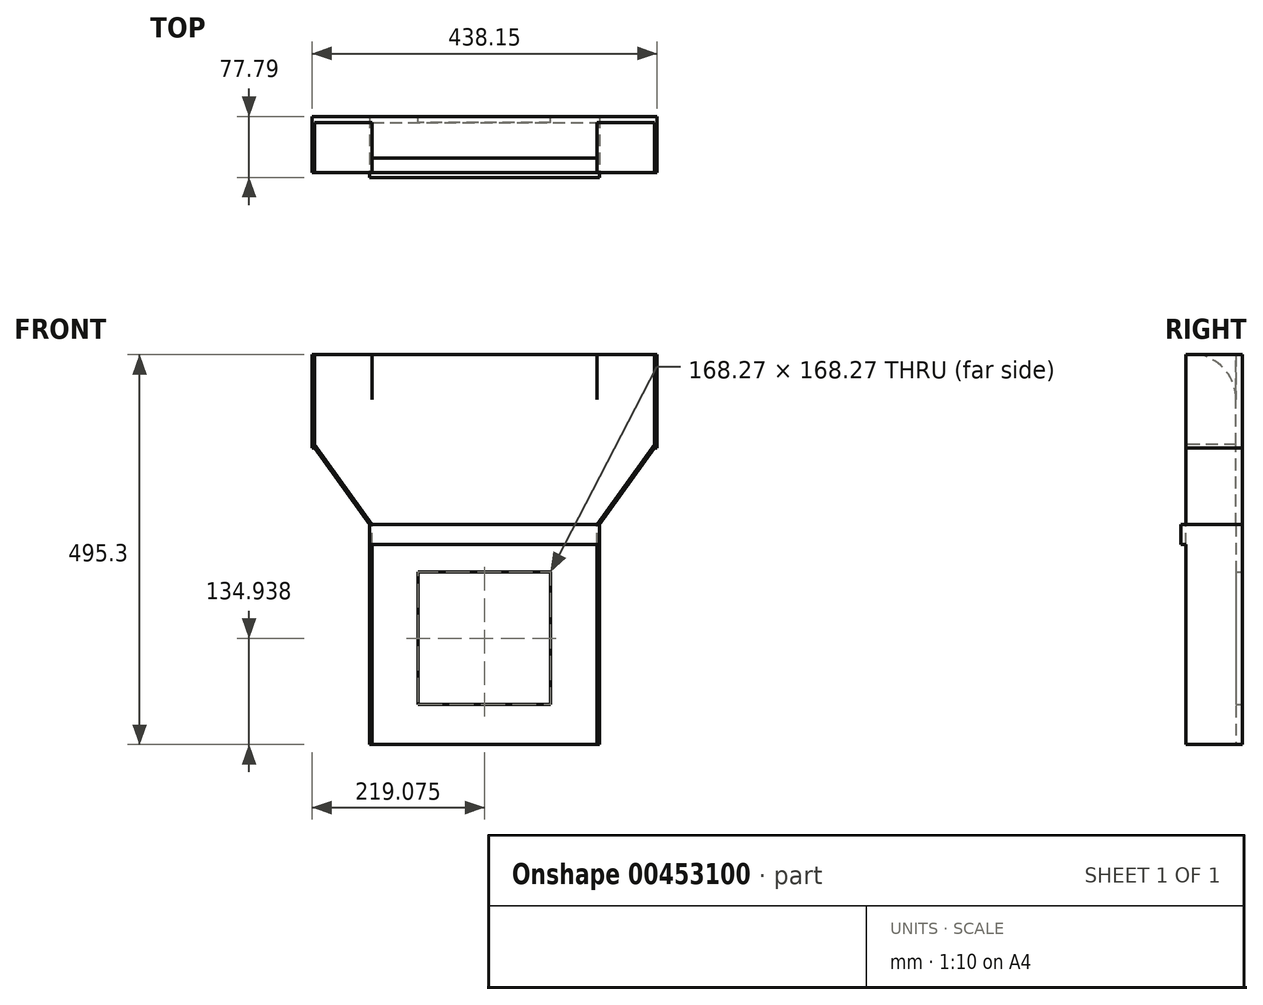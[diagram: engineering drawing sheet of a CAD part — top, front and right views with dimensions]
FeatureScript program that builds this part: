
annotation { "Feature Type Name" : "Feature", "Feature Type Description" : "" }
export const myFeature = defineFeature(function(context is Context, id is Id, definition is map)
    precondition{}
    {
        {
            var Q0;
            Q0=qCreatedBy(makeId("Front.planeOp"),FACE);
            var sketch = newSketch(context, id + "F0", { "sketchPlane" : qUnion([Q0])});
            skLineSegment(sketch, "E0.bottom", {"start": v(0, 0) * mm, "end": v(285.75, 0) * mm});
            skLineSegment(sketch, "E0.top", {"start": v(0, 279.4) * mm, "end": v(285.75, 279.4) * mm});
            skLineSegment(sketch, "E0.left", {"start": v(0, 0) * mm, "end": v(0, 279.4) * mm});
            skLineSegment(sketch, "E0.right", {"start": v(285.75, 0) * mm, "end": v(285.75, 279.4) * mm});
            skSolve(sketch);
        }
        {
            var Q0;
            Q0=makeQuery(id+"F0.imprint","IMPRINT",FACE,{"disambiguationData":[TD([[makeQuery(id+"F0.imprint","IMPRINT",EDGE,{"derivedFrom":sQuery(id+"F0.wireOp",EDGE,"E0.bottom")}),1.0]])]});
            extrude(context, id + "F1", {"entities" : qUnion([Q0]), "depth" : 3.17 * mm});
        }
        {
            var Q0;
            Q0=makeQuery(id+"F1.opExtrude","SWEPT_FACE",FACE,{"disambiguationData":[OSD([sQuery(id+"F0.wireOp",EDGE,"E0.top")])]});
            var sketch = newSketch(context, id + "F2", { "sketchPlane" : qUnion([Q0])});
            skLineSegment(sketch, "E1.bottom", {"start": v(0, 0) * mm, "end": v(285.75, 0) * mm});
            skLineSegment(sketch, "E1.top", {"start": v(0, -66.67) * mm, "end": v(285.75, -66.67) * mm});
            skLineSegment(sketch, "E1.left", {"start": v(0, 0) * mm, "end": v(0, -66.67) * mm});
            skLineSegment(sketch, "E1.right", {"start": v(285.75, 0) * mm, "end": v(285.75, -66.67) * mm});
            skSolve(sketch);
        }
        {
            var Q0;
            Q0 = qSketchRegion(id + "F2", true);
            extrude(context, id + "F3", {"entities" : qUnion([Q0]), "operationType" : NewBodyOperationType.ADD, "depth" : 215.9 * mm});
        }
        {
            var Q0;
            Q0=makeQuery(id+"F3.boolean.opBoolean","MERGE",FACE,{"derivedFrom":[makeQuery(id+"F1.opExtrude","SWEPT_FACE",FACE,{"disambiguationData":[OSD([sQuery(id+"F0.wireOp",EDGE,"E0.right")])]}),makeQuery(id+"F3.opExtrude","SWEPT_FACE",FACE,{"disambiguationData":[OSD([sQuery(id+"F2.wireOp",EDGE,"E1.right")])]})]});
            var sketch = newSketch(context, id + "F4", { "sketchPlane" : qUnion([Q0])});
            skLineSegment(sketch, "E2", {"start": v(-66.67, 495.3) * mm, "end": v(-66.67, 438.15) * mm});
            skLineSegment(sketch, "E3", {"start": v(-66.67, 438.15) * mm, "end": v(-7.94, 438.15) * mm});
            skCircle(sketch, "E4", {"center": v(-66.67, 438.15) * mm, "radius": 58.74 * mm});
            skLineSegment(sketch, "E5.bottom", {"start": v(-66.67, 379.41) * mm, "end": v(-7.94, 379.41) * mm});
            skLineSegment(sketch, "E5.top", {"start": v(-66.67, 279.4) * mm, "end": v(-7.94, 279.4) * mm});
            skLineSegment(sketch, "E5.left", {"start": v(-66.67, 379.41) * mm, "end": v(-66.67, 279.4) * mm});
            skLineSegment(sketch, "E5.right", {"start": v(-7.94, 379.41) * mm, "end": v(-7.94, 279.4) * mm});
            skLineSegment(sketch, "E6", {"start": v(-7.94, 438.15) * mm, "end": v(-7.94, 379.41) * mm});
            skSolve(sketch);
        }
        {
            var Q0;
            Q0=makeQuery(id+"F4.imprint","IMPRINT",FACE,{"disambiguationData":[TD([[makeQuery(id+"F4.imprint","IMPRINT",EDGE,{"derivedFrom":sQuery(id+"F4.wireOp",EDGE,"E5.bottom")}),-1.0]])]});
            var Q1;
            {var subQ2=sQuery(id+"F4.wireOp",EDGE,"E5.bottom");Q1=makeQuery(id+"F4.imprint","IMPRINT",FACE,{"disambiguationData":[TD([[makeQuery(id+"F4.imprint","IMPRINT",EDGE,{"derivedFrom":subQ2}),1.0]])]});}
            var Q2;
            {var subQ0=sQuery(id+"F4.wireOp",EDGE,"E3");Q2=makeQuery(id+"F4.imprint","IMPRINT",FACE,{"disambiguationData":[TD([[makeQuery(id+"F4.imprint","IMPRINT",EDGE,{"derivedFrom":subQ0}),-1.0]])]});}
            var Q3;
            {var subQ0=sQuery(id+"F4.wireOp",EDGE,"E2");Q3=makeQuery(id+"F4.imprint","IMPRINT",FACE,{"disambiguationData":[TD([[makeQuery(id+"F4.imprint","IMPRINT",EDGE,{"derivedFrom":subQ0}),1.0]])]});}
            extrude(context, id + "F5", {"entities" : qUnion([Q0, Q1, Q2, Q3]), "operationType" : NewBodyOperationType.REMOVE, "oppositeDirection" : true, "depth" : 285.75 * mm});
        }
        {
            var Q0;
            Q0=makeQuery(id+"F3.opExtrude","CAP_FACE",FACE,{"disambiguationData":[OSD([sQuery(id+"F2.wireOp",EDGE,"E1.bottom"),sQuery(id+"F2.wireOp",EDGE,"E1.top"),sQuery(id+"F2.wireOp",EDGE,"E1.left"),sQuery(id+"F2.wireOp",EDGE,"E1.right")])],"isStart":true});
            var sketch = newSketch(context, id + "F6", { "sketchPlane" : qUnion([Q0])});
            skLineSegment(sketch, "E7.bottom", {"start": v(0, 7.94) * mm, "end": v(285.75, 7.94) * mm});
            skLineSegment(sketch, "E7.top", {"start": v(0, 3.18) * mm, "end": v(285.75, 3.18) * mm});
            skLineSegment(sketch, "E7.left", {"start": v(0, 7.94) * mm, "end": v(0, 3.18) * mm});
            skLineSegment(sketch, "E7.right", {"start": v(285.75, 7.94) * mm, "end": v(285.75, 3.18) * mm});
            skSolve(sketch);
        }
        {
            var Q0;
            Q0=makeQuery(id+"F6.imprint","IMPRINT",FACE,{"disambiguationData":[TD([[makeQuery(id+"F6.imprint","IMPRINT",EDGE,{"derivedFrom":sQuery(id+"F6.wireOp",EDGE,"E7.bottom")}),-1.0]])]});
            extrude(context, id + "F7", {"entities" : qUnion([Q0]), "operationType" : NewBodyOperationType.ADD, "depth" : 279.4 * mm});
        }
        {
            var Q0;
            Q0=makeQuery(id+"F3.boolean.opBoolean","MERGE",FACE,{"derivedFrom":[makeQuery(id+"F1.opExtrude","CAP_FACE",FACE,{"disambiguationData":[OSD([sQuery(id+"F0.wireOp",EDGE,"E0.bottom"),sQuery(id+"F0.wireOp",EDGE,"E0.top"),sQuery(id+"F0.wireOp",EDGE,"E0.left"),sQuery(id+"F0.wireOp",EDGE,"E0.right")])],"isStart":true}),makeQuery(id+"F3.opExtrude","SWEPT_FACE",FACE,{"disambiguationData":[OSD([sQuery(id+"F2.wireOp",EDGE,"E1.bottom")])]})]});
            var sketch = newSketch(context, id + "F8", { "sketchPlane" : qUnion([Q0])});
            skLineSegment(sketch, "E8", {"start": v(-142.88, 0) * mm, "end": v(-142.88, 50.8) * mm});
            skLineSegment(sketch, "E9", {"start": v(-142.88, 50.8) * mm, "end": v(0, 50.8) * mm});
            skLineSegment(sketch, "E10", {"start": v(-142.88, 50.8) * mm, "end": v(-285.75, 50.8) * mm});
            skLineSegment(sketch, "E11", {"start": v(-285.75, 50.8) * mm, "end": v(-227.01, 50.8) * mm});
            skLineSegment(sketch, "E12", {"start": v(0, 50.8) * mm, "end": v(-58.74, 50.8) * mm});
            skLineSegment(sketch, "E13.bottom", {"start": v(-227.01, 50.8) * mm, "end": v(-58.74, 50.8) * mm});
            skLineSegment(sketch, "E13.top", {"start": v(-227.01, 219.08) * mm, "end": v(-58.74, 219.08) * mm});
            skLineSegment(sketch, "E13.left", {"start": v(-227.01, 50.8) * mm, "end": v(-227.01, 219.08) * mm});
            skLineSegment(sketch, "E13.right", {"start": v(-58.74, 50.8) * mm, "end": v(-58.74, 219.08) * mm});
            skSolve(sketch);
        }
        {
            var Q0;
            Q0=makeQuery(id+"F8.imprint","IMPRINT",FACE,{"disambiguationData":[TD([[makeQuery(id+"F8.imprint","IMPRINT",EDGE,{"derivedFrom":sQuery(id+"F8.wireOp",EDGE,"E13.top")}),-1.0]])]});
            extrude(context, id + "F9", {"entities" : qUnion([Q0]), "operationType" : NewBodyOperationType.REMOVE, "oppositeDirection" : true, "depth" : 25.4 * mm});
        }
        {
            var Q0;
            Q0=makeQuery(id+"F7.boolean.opBoolean","MERGE",FACE,{"derivedFrom":[makeQuery(id+"F3.boolean.opBoolean","MERGE",FACE,{"derivedFrom":[makeQuery(id+"F1.opExtrude","SWEPT_FACE",FACE,{"disambiguationData":[OSD([sQuery(id+"F0.wireOp",EDGE,"E0.right")])]}),makeQuery(id+"F3.opExtrude","SWEPT_FACE",FACE,{"disambiguationData":[OSD([sQuery(id+"F2.wireOp",EDGE,"E1.right")])]})]}),makeQuery(id+"F7.opExtrude","SWEPT_FACE",FACE,{"disambiguationData":[OSD([sQuery(id+"F6.wireOp",EDGE,"E7.right")])]})]});
            var sketch = newSketch(context, id + "F10", { "sketchPlane" : qUnion([Q0])});
            skLineSegment(sketch, "E14.bottom", {"start": v(0, 0) * mm, "end": v(-71.44, 0) * mm});
            skLineSegment(sketch, "E14.top", {"start": v(0, 279.4) * mm, "end": v(-71.44, 279.4) * mm});
            skLineSegment(sketch, "E14.left", {"start": v(0, 0) * mm, "end": v(0, 279.4) * mm});
            skLineSegment(sketch, "E14.right", {"start": v(-71.44, 0) * mm, "end": v(-71.44, 279.4) * mm});
            skSolve(sketch);
        }
        {
            var Q0;
            {var subQ3=sQuery(id+"F10.wireOp",EDGE,"E14.right");Q0=makeQuery(id+"F10.imprint","IMPRINT",FACE,{"disambiguationData":[TD([[makeQuery(id+"F10.imprint","IMPRINT",EDGE,{"derivedFrom":subQ3}),-1.0]])]});}
            var Q1;
            {var subQ0=sQuery(id+"F10.wireOp",EDGE,"E14.left");Q1=makeQuery(id+"F10.imprint","IMPRINT",FACE,{"disambiguationData":[TD([[makeQuery(id+"F10.imprint","IMPRINT",EDGE,{"derivedFrom":subQ0}),1.0]])]});}
            extrude(context, id + "F11", {"entities" : qUnion([Q0, Q1]), "operationType" : NewBodyOperationType.ADD, "depth" : 3.17 * mm});
        }
        {
            var Q0;
            Q0=makeQuery(id+"F7.boolean.opBoolean","MERGE",FACE,{"derivedFrom":[makeQuery(id+"F3.boolean.opBoolean","MERGE",FACE,{"derivedFrom":[makeQuery(id+"F1.opExtrude","SWEPT_FACE",FACE,{"disambiguationData":[OSD([sQuery(id+"F0.wireOp",EDGE,"E0.left")])]}),makeQuery(id+"F3.opExtrude","SWEPT_FACE",FACE,{"disambiguationData":[OSD([sQuery(id+"F2.wireOp",EDGE,"E1.left")])]})]}),makeQuery(id+"F7.opExtrude","SWEPT_FACE",FACE,{"disambiguationData":[OSD([sQuery(id+"F6.wireOp",EDGE,"E7.left")])]})]});
            var sketch = newSketch(context, id + "F12", { "sketchPlane" : qUnion([Q0])});
            skLineSegment(sketch, "E15.bottom", {"start": v(0, 0) * mm, "end": v(71.44, 0) * mm});
            skLineSegment(sketch, "E15.top", {"start": v(0, 279.4) * mm, "end": v(71.44, 279.4) * mm});
            skLineSegment(sketch, "E15.left", {"start": v(0, 0) * mm, "end": v(0, 279.4) * mm});
            skLineSegment(sketch, "E15.right", {"start": v(71.44, 0) * mm, "end": v(71.44, 279.4) * mm});
            skSolve(sketch);
        }
        {
            var Q0;
            {var subQ3=sQuery(id+"F12.wireOp",EDGE,"E15.right");Q0=makeQuery(id+"F12.imprint","IMPRINT",FACE,{"disambiguationData":[TD([[makeQuery(id+"F12.imprint","IMPRINT",EDGE,{"derivedFrom":subQ3}),1.0]])]});}
            var Q1;
            {var subQ0=sQuery(id+"F12.wireOp",EDGE,"E15.left");Q1=makeQuery(id+"F12.imprint","IMPRINT",FACE,{"disambiguationData":[TD([[makeQuery(id+"F12.imprint","IMPRINT",EDGE,{"derivedFrom":subQ0}),-1.0]])]});}
            extrude(context, id + "F13", {"entities" : qUnion([Q0, Q1]), "operationType" : NewBodyOperationType.ADD, "depth" : 3.17 * mm});
        }
        {
            var Q0;
            Q0=makeQuery(id+"F13.opExtrude","SWEPT_FACE",FACE,{"disambiguationData":[OSD([sQuery(id+"F12.wireOp",EDGE,"E15.top")])]});
            var sketch = newSketch(context, id + "F14", { "sketchPlane" : qUnion([Q0])});
            skLineSegment(sketch, "E16.bottom", {"start": v(0, 0) * mm, "end": v(-73.03, 0) * mm});
            skLineSegment(sketch, "E16.top", {"start": v(0, -71.44) * mm, "end": v(-73.02, -71.44) * mm});
            skLineSegment(sketch, "E16.left", {"start": v(0, 0) * mm, "end": v(0, -71.44) * mm});
            skLineSegment(sketch, "E16.right", {"start": v(-73.03, 0) * mm, "end": v(-73.02, -71.44) * mm});
            skSolve(sketch);
        }
        {
            var Q0;
            {var subQ6=makeQuery(id+"F13.opExtrude","CAP_EDGE",EDGE,{"disambiguationData":[OSD([sQuery(id+"F12.wireOp",EDGE,"E15.top")])],"isStart":false});Q0=makeQuery(id+"F14.imprint","IMPRINT",FACE,{"disambiguationData":[TD([[makeQuery(id+"F14.imprint","IMPRINT",EDGE,{"derivedFrom":subQ6}),1.0]])]});}
            var Q1;
            {var subQ2=sQuery(id+"F14.wireOp",EDGE,"E16.right");Q1=makeQuery(id+"F14.imprint","IMPRINT",FACE,{"disambiguationData":[TD([[makeQuery(id+"F14.imprint","IMPRINT",EDGE,{"derivedFrom":subQ2}),1.0]])]});}
            extrude(context, id + "F15", {"entities" : qUnion([Q0, Q1]), "operationType" : NewBodyOperationType.ADD, "depth" : 101.6 * mm});
        }
        {
            var Q0;
            Q0=makeQuery(id+"F15.boolean.opBoolean","MERGE",FACE,{"derivedFrom":[makeQuery(id+"F13.opExtrude","SWEPT_FACE",FACE,{"disambiguationData":[OSD([sQuery(id+"F12.wireOp",EDGE,"E15.right")])]}),makeQuery(id+"F15.opExtrude","SWEPT_FACE",FACE,{"disambiguationData":[OSD([sQuery(id+"F14.wireOp",EDGE,"E16.top")])]})]});
            var sketch = newSketch(context, id + "F16", { "sketchPlane" : qUnion([Q0])});
            skLineSegment(sketch, "E17", {"start": v(-3.18, 279.4) * mm, "end": v(0, 279.4) * mm});
            skLineSegment(sketch, "E18", {"start": v(0, 279.4) * mm, "end": v(-73.02, 381) * mm});
            skLineSegment(sketch, "E19", {"start": v(-73.02, 381) * mm, "end": v(-73.02, 279.4) * mm});
            skLineSegment(sketch, "E20", {"start": v(-3.17, 279.4) * mm, "end": v(-73.03, 376.58) * mm});
            skLineSegment(sketch, "E21", {"start": v(-40.23, 330.96) * mm, "end": v(-38.14, 332.46) * mm});
            skSolve(sketch);
        }
        {
            var Q0;
            {var subQ1=makeQuery(id+"F15.opExtrude","CAP_EDGE",EDGE,{"disambiguationData":[OSD([sQuery(id+"F14.wireOp",EDGE,"E16.top")])],"isStart":true});Q0=makeQuery(id+"F16.imprint","IMPRINT",FACE,{"disambiguationData":[TD([[makeQuery(id+"F16.imprint","IMPRINT",EDGE,{"derivedFrom":subQ1}),1.0]])]});}
            var Q1;
            {var subQ1=sQuery(id+"F14.wireOp",EDGE,"E16.top");var subQ5=makeQuery(id+"F15.opExtrude","CAP_EDGE",EDGE,{"disambiguationData":[OSD([subQ1])],"isStart":false});Q1=makeQuery(id+"F16.imprint","IMPRINT",FACE,{"disambiguationData":[TD([[makeQuery(id+"F16.imprint","IMPRINT",EDGE,{"derivedFrom":subQ5}),-1.0]])]});}
            extrude(context, id + "F17", {"entities" : qUnion([Q0, Q1]), "operationType" : NewBodyOperationType.REMOVE, "oppositeDirection" : true, "depth" : 71.44 * mm});
        }
        {
            var Q0;
            Q0=makeQuery(id+"F11.opExtrude","SWEPT_FACE",FACE,{"disambiguationData":[OSD([sQuery(id+"F10.wireOp",EDGE,"E14.top")])]});
            var sketch = newSketch(context, id + "F18", { "sketchPlane" : qUnion([Q0])});
            skLineSegment(sketch, "E22.bottom", {"start": v(285.75, 0) * mm, "end": v(358.78, 0) * mm});
            skLineSegment(sketch, "E22.top", {"start": v(285.75, -71.44) * mm, "end": v(358.78, -71.44) * mm});
            skLineSegment(sketch, "E22.left", {"start": v(285.75, 0) * mm, "end": v(285.75, -71.44) * mm});
            skLineSegment(sketch, "E22.right", {"start": v(358.78, 0) * mm, "end": v(358.78, -71.44) * mm});
            skSolve(sketch);
        }
        {
            var Q0;
            {var subQ6=makeQuery(id+"F11.opExtrude","CAP_EDGE",EDGE,{"disambiguationData":[OSD([sQuery(id+"F10.wireOp",EDGE,"E14.top")])],"isStart":false});Q0=makeQuery(id+"F18.imprint","IMPRINT",FACE,{"disambiguationData":[TD([[makeQuery(id+"F18.imprint","IMPRINT",EDGE,{"derivedFrom":subQ6}),-1.0]])]});}
            var Q1;
            {var subQ2=sQuery(id+"F18.wireOp",EDGE,"E22.right");Q1=makeQuery(id+"F18.imprint","IMPRINT",FACE,{"disambiguationData":[TD([[makeQuery(id+"F18.imprint","IMPRINT",EDGE,{"derivedFrom":subQ2}),-1.0]])]});}
            extrude(context, id + "F19", {"entities" : qUnion([Q0, Q1]), "operationType" : NewBodyOperationType.ADD, "depth" : 101.6 * mm});
        }
        {
            var Q0;
            Q0=makeQuery(id+"F19.boolean.opBoolean","MERGE",FACE,{"derivedFrom":[makeQuery(id+"F11.opExtrude","SWEPT_FACE",FACE,{"disambiguationData":[OSD([sQuery(id+"F10.wireOp",EDGE,"E14.right")])]}),makeQuery(id+"F19.opExtrude","SWEPT_FACE",FACE,{"disambiguationData":[OSD([sQuery(id+"F18.wireOp",EDGE,"E22.top")])]})]});
            var sketch = newSketch(context, id + "F20", { "sketchPlane" : qUnion([Q0])});
            skLineSegment(sketch, "E23", {"start": v(288.93, 279.4) * mm, "end": v(285.75, 279.4) * mm});
            skLineSegment(sketch, "E24", {"start": v(285.75, 279.4) * mm, "end": v(358.78, 381) * mm});
            skLineSegment(sketch, "E25", {"start": v(288.93, 279.4) * mm, "end": v(358.78, 376.58) * mm});
            skLineSegment(sketch, "E26", {"start": v(324.75, 333.66) * mm, "end": v(326.84, 332.16) * mm});
            skSolve(sketch);
        }
        {
            var Q0;
            {var subQ1=sQuery(id+"F18.wireOp",EDGE,"E22.top");var subQ5=makeQuery(id+"F19.opExtrude","CAP_EDGE",EDGE,{"disambiguationData":[OSD([subQ1])],"isStart":false});Q0=makeQuery(id+"F20.imprint","IMPRINT",FACE,{"disambiguationData":[TD([[makeQuery(id+"F20.imprint","IMPRINT",EDGE,{"derivedFrom":subQ5}),1.0]])]});}
            var Q1;
            {var subQ1=sQuery(id+"F18.wireOp",EDGE,"E22.top");var subQ2=makeQuery(id+"F19.opExtrude","CAP_EDGE",EDGE,{"disambiguationData":[OSD([subQ1])],"isStart":true});Q1=makeQuery(id+"F20.imprint","IMPRINT",FACE,{"disambiguationData":[TD([[makeQuery(id+"F20.imprint","IMPRINT",EDGE,{"derivedFrom":subQ2}),-1.0]])]});}
            extrude(context, id + "F21", {"entities" : qUnion([Q0, Q1]), "operationType" : NewBodyOperationType.REMOVE, "oppositeDirection" : true, "depth" : 71.44 * mm});
        }
        {
            var Q0;
            Q0=makeQuery(id+"F19.opExtrude","SWEPT_FACE",FACE,{"disambiguationData":[OSD([sQuery(id+"F18.wireOp",EDGE,"E22.right")])]});
            var sketch = newSketch(context, id + "F22", { "sketchPlane" : qUnion([Q0])});
            skLineSegment(sketch, "E27.bottom", {"start": v(-71.44, 381) * mm, "end": v(0, 381) * mm});
            skLineSegment(sketch, "E27.top", {"start": v(-71.44, 495.3) * mm, "end": v(0, 495.3) * mm});
            skLineSegment(sketch, "E27.left", {"start": v(-71.44, 381) * mm, "end": v(-71.44, 495.3) * mm});
            skLineSegment(sketch, "E27.right", {"start": v(0, 381) * mm, "end": v(0, 495.3) * mm});
            skLineSegment(sketch, "E28.top", {"start": v(-71.44, 376.58) * mm, "end": v(0, 376.58) * mm});
            skLineSegment(sketch, "E28.left", {"start": v(-71.44, 381) * mm, "end": v(-71.44, 376.58) * mm});
            skLineSegment(sketch, "E28.right", {"start": v(0, 381) * mm, "end": v(0, 376.58) * mm});
            skSolve(sketch);
        }
        {
            var Q0;
            Q0=makeQuery(id+"F15.opExtrude","SWEPT_FACE",FACE,{"disambiguationData":[OSD([sQuery(id+"F14.wireOp",EDGE,"E16.right")])]});
            var sketch = newSketch(context, id + "F23", { "sketchPlane" : qUnion([Q0])});
            skLineSegment(sketch, "E29.bottom", {"start": v(0, 381) * mm, "end": v(71.44, 381) * mm});
            skLineSegment(sketch, "E29.top", {"start": v(0, 495.3) * mm, "end": v(71.44, 495.3) * mm});
            skLineSegment(sketch, "E29.left", {"start": v(0, 381) * mm, "end": v(0, 495.3) * mm});
            skLineSegment(sketch, "E29.right", {"start": v(71.44, 381) * mm, "end": v(71.44, 495.3) * mm});
            skLineSegment(sketch, "E30.top", {"start": v(0, 376.58) * mm, "end": v(71.44, 376.58) * mm});
            skLineSegment(sketch, "E30.left", {"start": v(0, 381) * mm, "end": v(0, 376.58) * mm});
            skLineSegment(sketch, "E30.right", {"start": v(71.44, 381) * mm, "end": v(71.44, 376.58) * mm});
            skSolve(sketch);
        }
        {
            var Q0;
            Q0=makeQuery(id+"FLgJ0Njv8MfhhJH_1.boolean.opBoolean","MERGE",FACE,{"derivedFrom":[makeQuery(id+"F15.boolean.opBoolean","MERGE",FACE,{"derivedFrom":[makeQuery(id+"F13.opExtrude","SWEPT_FACE",FACE,{"disambiguationData":[OSD([sQuery(id+"F12.wireOp",EDGE,"E15.right")])]}),makeQuery(id+"F15.opExtrude","SWEPT_FACE",FACE,{"disambiguationData":[OSD([sQuery(id+"F14.wireOp",EDGE,"E16.top")])]})]}),makeQuery(id+"FLgJ0Njv8MfhhJH_1.opExtrude","SWEPT_FACE",FACE,{"disambiguationData":[OSD([sQuery(id+"F23.wireOp",EDGE,"DmIn1l5T-Cbd6-dnzl-y2dn-FXteETVq3aXz.right")])]})]});
            var sketch = newSketch(context, id + "F24", { "sketchPlane" : qUnion([Q0])});
            skLineSegment(sketch, "E31.bottom", {"start": v(-3.18, 279.4) * mm, "end": v(288.93, 279.4) * mm});
            skLineSegment(sketch, "E31.top", {"start": v(-3.18, 254) * mm, "end": v(288.93, 254) * mm});
            skLineSegment(sketch, "E31.left", {"start": v(-3.18, 279.4) * mm, "end": v(-3.18, 254) * mm});
            skLineSegment(sketch, "E31.right", {"start": v(288.93, 279.4) * mm, "end": v(288.93, 254) * mm});
            skSolve(sketch);
        }
        {
            var Q0;
            {var subQ0=sQuery(id+"F24.wireOp",EDGE,"E31.left");Q0=makeQuery(id+"F24.imprint","IMPRINT",FACE,{"disambiguationData":[TD([[makeQuery(id+"F24.imprint","IMPRINT",EDGE,{"derivedFrom":subQ0}),-1.0]])]});}
            var Q1;
            {var subQ3=sQuery(id+"F24.wireOp",EDGE,"E31.right");Q1=makeQuery(id+"F24.imprint","IMPRINT",FACE,{"disambiguationData":[TD([[makeQuery(id+"F24.imprint","IMPRINT",EDGE,{"derivedFrom":subQ3}),-1.0]])]});}
            extrude(context, id + "F25", {"entities" : qUnion([Q0, Q1]), "operationType" : NewBodyOperationType.ADD, "depth" : 6.35 * mm});
        }
        {
            var Q0;
            Q0 = qSketchRegion(id + "F22", true);
            extrude(context, id + "F26", {"entities" : qUnion([Q0]), "operationType" : NewBodyOperationType.ADD, "depth" : 3.17 * mm});
        }
        {
            var Q0;
            Q0=makeQuery(id+"F23.imprint","IMPRINT",FACE,{"disambiguationData":[TD([[makeQuery(id+"F23.imprint","IMPRINT",EDGE,{"derivedFrom":sQuery(id+"F23.wireOp",EDGE,"E29.bottom")}),-1.0]])]});
            var Q1;
            Q1=makeQuery(id+"F23.imprint","IMPRINT",FACE,{"disambiguationData":[TD([[makeQuery(id+"F23.imprint","IMPRINT",EDGE,{"derivedFrom":sQuery(id+"F23.wireOp",EDGE,"E29.top")}),-1.0]])]});
            extrude(context, id + "F27", {"entities" : qUnion([Q0, Q1]), "operationType" : NewBodyOperationType.ADD, "depth" : 3.17 * mm});
        }
        {
            var Q0;
            Q0=makeQuery(id+"F17.boolean.opBoolean","MERGE",FACE,{"derivedFrom":[makeQuery(id+"F7.boolean.opBoolean","MERGE",FACE,{"derivedFrom":[makeQuery(id+"F3.boolean.opBoolean","MERGE",FACE,{"derivedFrom":[makeQuery(id+"F1.opExtrude","SWEPT_FACE",FACE,{"disambiguationData":[OSD([sQuery(id+"F0.wireOp",EDGE,"E0.left")])]}),makeQuery(id+"F3.opExtrude","SWEPT_FACE",FACE,{"disambiguationData":[OSD([sQuery(id+"F2.wireOp",EDGE,"E1.left")])]})]}),makeQuery(id+"F7.opExtrude","SWEPT_FACE",FACE,{"disambiguationData":[OSD([sQuery(id+"F6.wireOp",EDGE,"E7.left")])]})]}),makeQuery(id+"F17.opExtrude","SWEPT_FACE",FACE,{"disambiguationData":[OSD([sQuery(id+"F12.wireOp",EDGE,"E15.right"),sQuery(id+"F14.wireOp",EDGE,"E16.top"),sQuery(id+"F14.wireOp",EDGE,"E16.left")])]})]});
            var sketch = newSketch(context, id + "F28", { "sketchPlane" : qUnion([Q0])});
            skLineSegment(sketch, "E32.bottom", {"start": v(0, 495.3) * mm, "end": v(7.94, 495.3) * mm});
            skLineSegment(sketch, "E32.top", {"start": v(0, 279.4) * mm, "end": v(7.94, 279.4) * mm});
            skLineSegment(sketch, "E32.left", {"start": v(0, 495.3) * mm, "end": v(0, 279.4) * mm});
            skLineSegment(sketch, "E32.right", {"start": v(7.94, 495.3) * mm, "end": v(7.94, 279.4) * mm});
            skSolve(sketch);
        }
        {
            var Q0;
            {var subQ3=sQuery(id+"F28.wireOp",EDGE,"E32.bottom");Q0=makeQuery(id+"F28.imprint","IMPRINT",FACE,{"disambiguationData":[TD([[makeQuery(id+"F28.imprint","IMPRINT",EDGE,{"derivedFrom":subQ3}),1.0]])]});}
            extrude(context, id + "F29", {"entities" : qUnion([Q0]), "operationType" : NewBodyOperationType.ADD, "depth" : 101.6 * mm});
        }
        {
            var Q0;
            Q0=makeQuery(id+"F29.boolean.opBoolean","SPLIT",FACE,{"derivedFrom":makeQuery(id+"F29.opExtrude","SWEPT_FACE",FACE,{"disambiguationData":[OSD([sQuery(id+"F28.wireOp",EDGE,"E32.right")])]})});
            var sketch = newSketch(context, id + "F30", { "sketchPlane" : qUnion([Q0])});
            skLineSegment(sketch, "E33", {"start": v(-76.2, 495.3) * mm, "end": v(-101.6, 495.3) * mm});
            skLineSegment(sketch, "E34", {"start": v(-101.6, 495.3) * mm, "end": v(-101.6, 279.4) * mm});
            skLineSegment(sketch, "E35", {"start": v(-101.6, 279.4) * mm, "end": v(-3.17, 279.4) * mm});
            skLineSegment(sketch, "E36", {"start": v(-3.17, 279.4) * mm, "end": v(-73.02, 376.58) * mm});
            skLineSegment(sketch, "E37", {"start": v(-73.02, 376.58) * mm, "end": v(-76.2, 376.58) * mm});
            skLineSegment(sketch, "E38", {"start": v(-76.2, 376.58) * mm, "end": v(-76.2, 495.3) * mm});
            skSolve(sketch);
        }
        {
            var Q0;
            Q0=makeQuery(id+"F30.imprint","IMPRINT",FACE,{"disambiguationData":[TD([[makeQuery(id+"F30.imprint","IMPRINT",EDGE,{"derivedFrom":sQuery(id+"F30.wireOp",EDGE,"E33")}),-1.0]])]});
            extrude(context, id + "F31", {"entities" : qUnion([Q0]), "operationType" : NewBodyOperationType.REMOVE, "oppositeDirection" : true, "depth" : 25.4 * mm});
        }
        {
            var Q0;
            Q0=makeQuery(id+"F21.boolean.opBoolean","MERGE",FACE,{"derivedFrom":[makeQuery(id+"F7.boolean.opBoolean","MERGE",FACE,{"derivedFrom":[makeQuery(id+"F3.boolean.opBoolean","MERGE",FACE,{"derivedFrom":[makeQuery(id+"F1.opExtrude","SWEPT_FACE",FACE,{"disambiguationData":[OSD([sQuery(id+"F0.wireOp",EDGE,"E0.right")])]}),makeQuery(id+"F3.opExtrude","SWEPT_FACE",FACE,{"disambiguationData":[OSD([sQuery(id+"F2.wireOp",EDGE,"E1.right")])]})]}),makeQuery(id+"F7.opExtrude","SWEPT_FACE",FACE,{"disambiguationData":[OSD([sQuery(id+"F6.wireOp",EDGE,"E7.right")])]})]}),makeQuery(id+"F21.opExtrude","SWEPT_FACE",FACE,{"disambiguationData":[OSD([sQuery(id+"F10.wireOp",EDGE,"E14.right"),sQuery(id+"F18.wireOp",EDGE,"E22.top"),sQuery(id+"F18.wireOp",EDGE,"E22.left")])]})]});
            var sketch = newSketch(context, id + "F32", { "sketchPlane" : qUnion([Q0])});
            skLineSegment(sketch, "E39.bottom", {"start": v(0, 495.3) * mm, "end": v(-7.94, 495.3) * mm});
            skLineSegment(sketch, "E39.top", {"start": v(0, 279.4) * mm, "end": v(-7.94, 279.4) * mm});
            skLineSegment(sketch, "E39.left", {"start": v(0, 495.3) * mm, "end": v(0, 279.4) * mm});
            skLineSegment(sketch, "E39.right", {"start": v(-7.94, 495.3) * mm, "end": v(-7.94, 279.4) * mm});
            skSolve(sketch);
        }
        {
            var Q0;
            {var subQ3=sQuery(id+"F32.wireOp",EDGE,"E39.bottom");Q0=makeQuery(id+"F32.imprint","IMPRINT",FACE,{"disambiguationData":[TD([[makeQuery(id+"F32.imprint","IMPRINT",EDGE,{"derivedFrom":subQ3}),-1.0]])]});}
            extrude(context, id + "F33", {"entities" : qUnion([Q0]), "operationType" : NewBodyOperationType.ADD, "depth" : 101.6 * mm});
        }
        {
            var Q0;
            Q0=makeQuery(id+"F33.boolean.opBoolean","SPLIT",FACE,{"derivedFrom":makeQuery(id+"F33.opExtrude","SWEPT_FACE",FACE,{"disambiguationData":[OSD([sQuery(id+"F32.wireOp",EDGE,"E39.right")])]})});
            var sketch = newSketch(context, id + "F34", { "sketchPlane" : qUnion([Q0])});
            skLineSegment(sketch, "E40", {"start": v(361.95, 495.3) * mm, "end": v(361.95, 376.58) * mm});
            skLineSegment(sketch, "E41", {"start": v(361.95, 376.58) * mm, "end": v(358.78, 376.58) * mm});
            skLineSegment(sketch, "E42", {"start": v(358.77, 376.58) * mm, "end": v(288.92, 279.4) * mm});
            skLineSegment(sketch, "E43", {"start": v(288.92, 279.4) * mm, "end": v(387.35, 279.4) * mm});
            skLineSegment(sketch, "E44", {"start": v(387.35, 279.4) * mm, "end": v(387.35, 495.3) * mm});
            skLineSegment(sketch, "E45", {"start": v(387.35, 495.3) * mm, "end": v(361.95, 495.3) * mm});
            skSolve(sketch);
        }
        {
            var Q0;
            Q0=makeQuery(id+"F34.imprint","IMPRINT",FACE,{"disambiguationData":[TD([[makeQuery(id+"F34.imprint","IMPRINT",EDGE,{"derivedFrom":sQuery(id+"F34.wireOp",EDGE,"E40")}),-1.0]])]});
            extrude(context, id + "F35", {"entities" : qUnion([Q0]), "operationType" : NewBodyOperationType.REMOVE, "oppositeDirection" : true, "depth" : 25.4 * mm});
        }
    });
